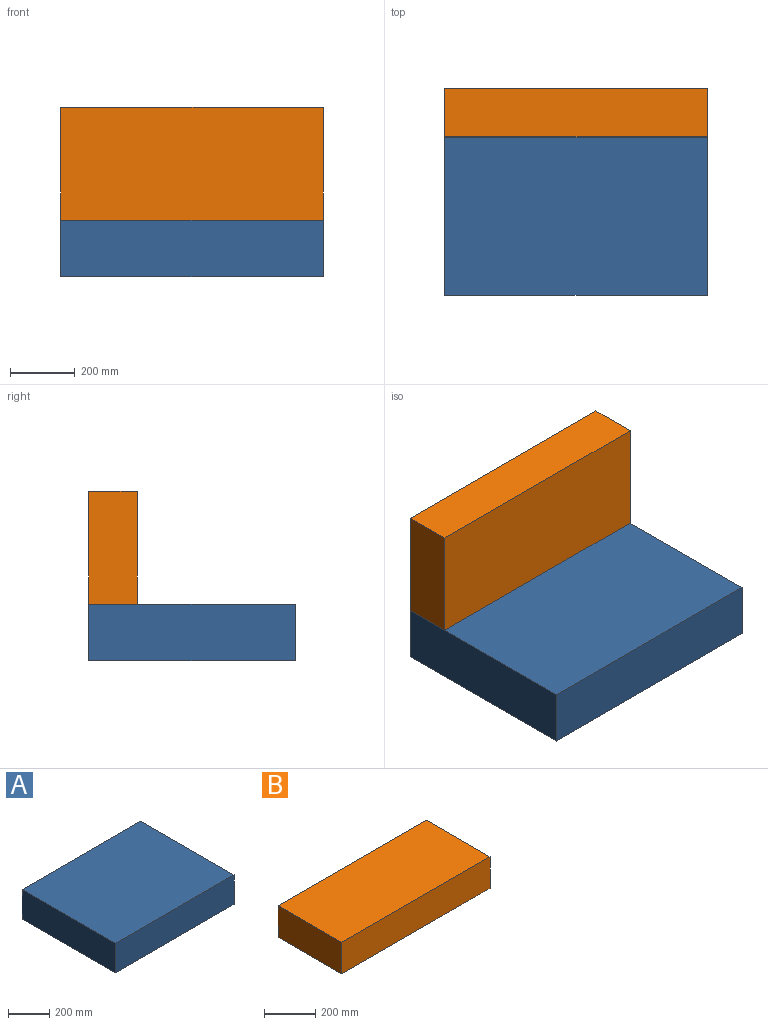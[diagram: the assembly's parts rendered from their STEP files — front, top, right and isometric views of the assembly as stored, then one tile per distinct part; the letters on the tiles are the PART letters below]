
ASSEMBLY  parts=2 mates=1
PART A: 6 faces, bbox 815x640x175 mm
  f0: plane 815x175mm, normal (0,1,0), area 142625mm2, adj f1,f3,f4,f5
  f1: plane 640x175mm, normal (-1,0,0), area 112000mm2, adj f0,f2,f4,f5
  f2: plane 815x175mm, normal (0,-1,0), area 142625mm2, adj f1,f3,f4,f5
  f3: plane 640x175mm, normal (1,0,0), area 112000mm2, adj f0,f2,f4,f5
  f4: plane 815x640mm, normal (0,0,1), area 521600mm2, adj f0,f1,f2,f3
  f5: plane 815x640mm, normal (0,0,-1), area 521600mm2, adj f0,f1,f2,f3
PART B: 6 faces, bbox 815x350x150 mm
  f0: plane 815x150mm, normal (0,-1,0), area 122250mm2, adj f1,f3,f4,f5
  f1: plane 350x150mm, normal (1,0,0), area 52500mm2, adj f0,f2,f4,f5
  f2: plane 815x150mm, normal (0,1,0), area 122250mm2, adj f1,f3,f4,f5
  f3: plane 350x150mm, normal (-1,0,0), area 52500mm2, adj f0,f2,f4,f5
  f4: plane 815x350mm, normal (0,0,1), area 285250mm2, adj f0,f1,f2,f3
  f5: plane 815x350mm, normal (0,0,-1), area 285250mm2, adj f0,f1,f2,f3
PLACE A t=(-597.44,-16.96,-167.09)mm
PLACE B rot(axis=(0,-0.71,0.71),180deg) t=(-476.36,228.64,-763.5)mm
MATE fastened B.f2 <-> A.f4  axis (0,0,-1) through (-944.4,228.64,7.91)mm
